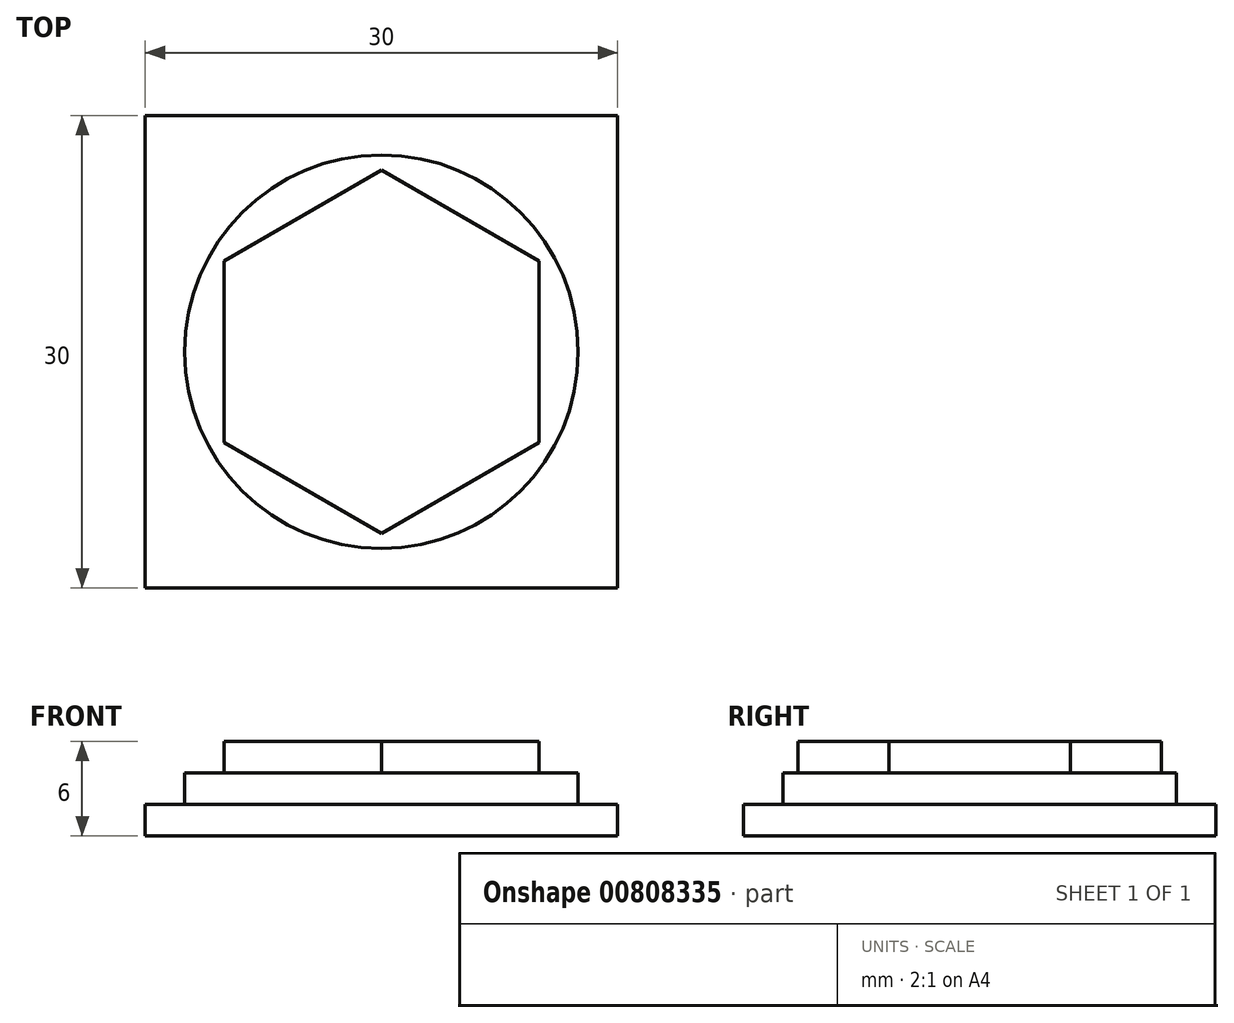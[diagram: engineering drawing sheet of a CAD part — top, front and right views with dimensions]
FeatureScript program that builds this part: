
annotation { "Feature Type Name" : "Feature", "Feature Type Description" : "" }
export const myFeature = defineFeature(function(context is Context, id is Id, definition is map)
    precondition{}
    {
        {
            var Q0;
            Q0=qCreatedBy(makeId("Top.planeOp"),FACE);
            var sketch = newSketch(context, id + "F0", { "sketchPlane" : qUnion([Q0])});
            skLineSegment(sketch, "E0.bottom", {"start": v(-15, 15) * mm, "end": v(15, 15) * mm});
            skLineSegment(sketch, "E0.top", {"start": v(-15, -15) * mm, "end": v(15, -15) * mm});
            skLineSegment(sketch, "E0.left", {"start": v(-15, 15) * mm, "end": v(-15, -15) * mm});
            skLineSegment(sketch, "E0.right", {"start": v(15, 15) * mm, "end": v(15, -15) * mm});
            skPoint(sketch, "E0.middle", {"position": v(0, 0) * mm});
            skSolve(sketch);
        }
        {
            var Q0;
            Q0 = qSketchRegion(id + "F0", true);
            extrude(context, id + "F1", {"entities" : qUnion([Q0]), "depth" : 2 * mm, "offsetDistance" : 25 * mm});
        }
        {
            var Q0;
            Q0=makeQuery(id+"F1.opExtrude","CAP_FACE",FACE,{"disambiguationData":[OSD([sQuery(id+"F0.wireOp",EDGE,"E0.bottom"),sQuery(id+"F0.wireOp",EDGE,"E0.top"),sQuery(id+"F0.wireOp",EDGE,"E0.left"),sQuery(id+"F0.wireOp",EDGE,"E0.right")])],"isStart":false});
            var sketch = newSketch(context, id + "F2", { "sketchPlane" : qUnion([Q0])});
            skCircle(sketch, "E1", {"center": v(0, 0) * mm, "radius": 12.5 * mm});
            skSolve(sketch);
        }
        {
            var Q0;
            Q0 = qSketchRegion(id + "F2", true);
            extrude(context, id + "F3", {"entities" : qUnion([Q0]), "operationType" : NewBodyOperationType.ADD, "depth" : 2 * mm, "offsetDistance" : 25 * mm});
        }
        {
            var Q0;
            Q0=makeQuery(id+"F3.opExtrude","CAP_FACE",FACE,{"disambiguationData":[OSD([sQuery(id+"F2.wireOp",EDGE,"E1")])],"isStart":false});
            var sketch = newSketch(context, id + "F4", { "sketchPlane" : qUnion([Q0])});
            skCircle(sketch, "E2.cCircle", {"center": v(0, 0) * mm, "radius": 10 * mm, "construction": true});
            skLineSegment(sketch, "E2.0", {"start": v(-10, 5.77) * mm, "end": v(0, 11.55) * mm});
            skLineSegment(sketch, "E2.1", {"start": v(0, 11.55) * mm, "end": v(10, 5.77) * mm});
            skLineSegment(sketch, "E2.2", {"start": v(10, 5.77) * mm, "end": v(10, -5.77) * mm});
            skLineSegment(sketch, "E2.3", {"start": v(10, -5.77) * mm, "end": v(0, -11.55) * mm});
            skLineSegment(sketch, "E2.4", {"start": v(0, -11.55) * mm, "end": v(-10, -5.77) * mm});
            skLineSegment(sketch, "E2.5", {"start": v(-10, -5.77) * mm, "end": v(-10, 5.77) * mm});
            skPoint(sketch, "E2.0.midPoint", {"position": v(-5, 8.66) * mm});
            skLineSegment(sketch, "E3", {"start": v(0, 19.27) * mm, "end": v(0, -18.68) * mm, "construction": true});
            skSolve(sketch);
        }
        {
            var Q0;
            Q0 = qSketchRegion(id + "F4", true);
            extrude(context, id + "F5", {"entities" : qUnion([Q0]), "operationType" : NewBodyOperationType.ADD, "depth" : 2 * mm, "offsetDistance" : 25 * mm});
        }
    });
